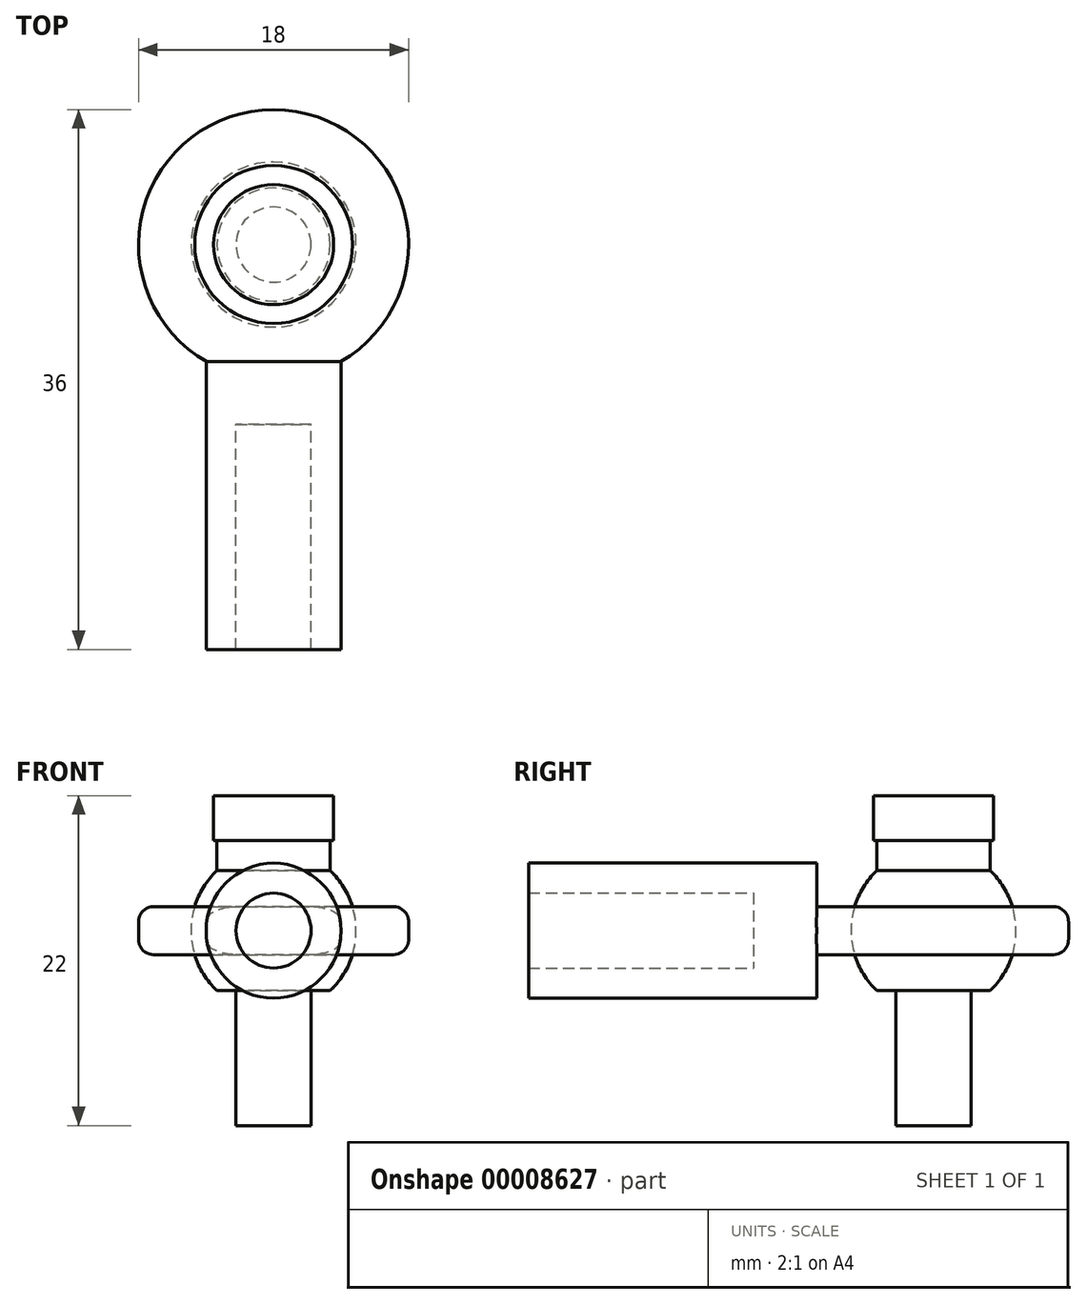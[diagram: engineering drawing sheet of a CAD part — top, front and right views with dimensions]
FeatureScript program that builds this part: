
annotation { "Feature Type Name" : "Feature", "Feature Type Description" : "" }
export const myFeature = defineFeature(function(context is Context, id is Id, definition is map)
    precondition{}
    {
        {
            var Q0;
            Q0=qCreatedBy(makeId("Right.planeOp"),FACE);
            var sketch = newSketch(context, id + "F0", { "sketchPlane" : qUnion([Q0])});
            skCircle(sketch, "E0", {"center": v(0, 0) * mm, "radius": 5.5 * mm});
            skLineSegment(sketch, "E1", {"start": v(-2.5, 4.9) * mm, "end": v(-2.5, -4.9) * mm});
            skLineSegment(sketch, "E2.MirrorCS", {"start": v(2.5, 4.9) * mm, "end": v(2.5, -4.9) * mm});
            skLineSegment(sketch, "E3", {"start": v(-2.5, 4) * mm, "end": v(-3.77, 4) * mm});
            skLineSegment(sketch, "E4.MirrorCS", {"start": v(-2.5, -4) * mm, "end": v(-3.77, -4) * mm});
            skLineSegment(sketch, "E5.MirrorCS", {"start": v(2.5, 4) * mm, "end": v(3.77, 4) * mm});
            skLineSegment(sketch, "E6.MirrorCS", {"start": v(2.5, -4) * mm, "end": v(3.77, -4) * mm});
            skLineSegment(sketch, "E7", {"start": v(0, 14.77) * mm, "end": v(0, -12.33) * mm, "construction": true});
            skLineSegment(sketch, "E8", {"start": v(-15.77, 0) * mm, "end": v(22.06, 0) * mm, "construction": true});
            skLineSegment(sketch, "E9", {"start": v(-9, 0) * mm, "end": v(-9, 1.6) * mm});
            skLineSegment(sketch, "E10", {"start": v(-9, 1.6) * mm, "end": v(-5.26, 1.6) * mm});
            skLineSegment(sketch, "E11.MirrorCS", {"start": v(-9, 0) * mm, "end": v(-9, -1.6) * mm});
            skLineSegment(sketch, "E12.MirrorCS", {"start": v(-9, -1.6) * mm, "end": v(-5.26, -1.6) * mm});
            skLineSegment(sketch, "E13.MirrorCS", {"start": v(9, 1.6) * mm, "end": v(5.26, 1.6) * mm});
            skLineSegment(sketch, "E14.MirrorCS", {"start": v(9, 0) * mm, "end": v(9, 1.6) * mm});
            skLineSegment(sketch, "E15.MirrorCS", {"start": v(9, 0) * mm, "end": v(9, -1.6) * mm});
            skLineSegment(sketch, "E16.MirrorCS", {"start": v(9, -1.6) * mm, "end": v(5.26, -1.6) * mm});
            skSolve(sketch);
        }
        {
            var Q0;
            {var subQ1=sQuery(id+"F0.wireOp",EDGE,"E3");Q0=makeQuery(id+"F0.imprint","IMPRINT",FACE,{"disambiguationData":[TD([[makeQuery(id+"F0.imprint","IMPRINT",EDGE,{"derivedFrom":subQ1}),1.0]])]});}
            var Q1;
            Q1=sQuery(id+"F0.wireOp",EDGE,"E7");
            revolve(context, id + "F1", {"entities" : qUnion([Q0]), "axis" : qUnion([Q1]), "revolveType" : RevolveType.FULL});
        }
        {
            var Q0;
            Q0=makeQuery(id+"F0.imprint","IMPRINT",FACE,{"disambiguationData":[TD([[makeQuery(id+"F0.imprint","IMPRINT",EDGE,{"derivedFrom":sQuery(id+"F0.wireOp",EDGE,"E9")}),-1.0]])]});
            var Q1;
            Q1=sQuery(id+"F0.wireOp",EDGE,"E7");
            revolve(context, id + "F2", {"entities" : qUnion([Q0]), "axis" : qUnion([Q1]), "revolveType" : RevolveType.FULL});
        }
        {
            var Q0;
            Q0=qCreatedBy(makeId("Top.planeOp"),FACE);
            var sketch = newSketch(context, id + "F3", { "sketchPlane" : qUnion([Q0])});
            skLineSegment(sketch, "E17", {"start": v(0, 0) * mm, "end": v(0, -27) * mm, "construction": true});
            skLineSegment(sketch, "E18", {"start": v(0, -27) * mm, "end": v(-4.5, -27) * mm});
            skLineSegment(sketch, "E19.MirrorCS", {"start": v(0, -27) * mm, "end": v(4.5, -27) * mm});
            skLineSegment(sketch, "E20", {"start": v(-2.5, -27) * mm, "end": v(-2.5, -12) * mm});
            skLineSegment(sketch, "E21", {"start": v(-2.5, -12) * mm, "end": v(0, -12) * mm});
            skLineSegment(sketch, "E22.MirrorCS", {"start": v(2.5, -12) * mm, "end": v(0, -12) * mm});
            skLineSegment(sketch, "E23.MirrorCS", {"start": v(2.5, -27) * mm, "end": v(2.5, -12) * mm});
            skCircle(sketch, "E24.0.0", {"center": v(0, 0) * mm, "radius": 9 * mm});
            skLineSegment(sketch, "E25", {"start": v(4.5, -27) * mm, "end": v(4.5, -7.8) * mm});
            skLineSegment(sketch, "E26", {"start": v(4.5, -7.8) * mm, "end": v(0, -7.8) * mm});
            skLineSegment(sketch, "E27.MirrorCS", {"start": v(-4.5, -7.8) * mm, "end": v(0, -7.8) * mm});
            skLineSegment(sketch, "E28.MirrorCS", {"start": v(-4.5, -27) * mm, "end": v(-4.5, -7.8) * mm});
            skLineSegment(sketch, "E29", {"start": v(0, -7.8) * mm, "end": v(0, -12) * mm});
            skSolve(sketch);
        }
        {
            var Q0;
            {var subQ3=sQuery(id+"F3.wireOp",EDGE,"E27.MirrorCS");Q0=makeQuery(id+"F3.imprint","IMPRINT",FACE,{"disambiguationData":[TD([[makeQuery(id+"F3.imprint","IMPRINT",EDGE,{"derivedFrom":subQ3}),-1.0]])]});}
            var Q1;
            {var subQ5=sQuery(id+"F3.wireOp",EDGE,"E20");Q1=makeQuery(id+"F3.imprint","IMPRINT",FACE,{"disambiguationData":[TD([[makeQuery(id+"F3.imprint","IMPRINT",EDGE,{"derivedFrom":subQ5}),1.0]])]});}
            var Q2;
            Q2=sQuery(id+"F3.wireOp",EDGE,"E17");
            revolve(context, id + "F4", {"operationType" : NewBodyOperationType.ADD, "entities" : qUnion([Q0, Q1]), "axis" : qUnion([Q2]), "revolveType" : RevolveType.FULL});
        }
        {
            var Q0;
            Q0=makeQuery(id+"F2.opRevolve","SWEPT_EDGE",EDGE,{"disambiguationData":[OSD([sQuery(id+"F0.wireOp",EDGE,"E9"),sQuery(id+"F0.wireOp",EDGE,"E10")])]});
            var Q1;
            Q1=makeQuery(id+"F2.opRevolve","SWEPT_EDGE",EDGE,{"disambiguationData":[OSD([sQuery(id+"F0.wireOp",EDGE,"E11.MirrorCS"),sQuery(id+"F0.wireOp",EDGE,"E12.MirrorCS")])]});
            fillet(context, id + "F5", {"entities" : qUnion([Q0, Q1]), "radius" : 1 * mm, "tangentPropagation" : true, "allowEdgeOverflow" : false});
        }
        {
            var Q0;
            Q0=makeQuery(id+"F1.opRevolve","SWEPT_FACE",FACE,{"disambiguationData":[OSD([sQuery(id+"F0.wireOp",EDGE,"E3")])]});
            extrude(context, id + "F6", {"entities" : qUnion([Q0]), "depth" : 2 * mm});
        }
        {
            var Q0;
            Q0=makeQuery(id+"F6.opExtrude","CAP_FACE",FACE,{"disambiguationData":[OSD([sQuery(id+"F0.wireOp",EDGE,"E3")])],"isStart":false});
            var sketch = newSketch(context, id + "F7", { "sketchPlane" : qUnion([Q0])});
            skCircle(sketch, "E30", {"center": v(0, 0) * mm, "radius": 2.5 * mm});
            skCircle(sketch, "E31", {"center": v(0, 0) * mm, "radius": 4 * mm});
            skSolve(sketch);
        }
        {
            var Q0;
            Q0=makeQuery(id+"F7.imprint","IMPRINT",FACE,{"disambiguationData":[TD([[makeQuery(id+"F7.imprint","IMPRINT",EDGE,{"derivedFrom":sQuery(id+"F7.wireOp",EDGE,"E31")}),1.0]])]});
            var Q1;
            Q1=makeQuery(id+"F7.imprint","IMPRINT",FACE,{"disambiguationData":[TD([[makeQuery(id+"F7.imprint","IMPRINT",EDGE,{"derivedFrom":sQuery(id+"F7.wireOp",EDGE,"E30")}),1.0]])]});
            var Q2;
            Q2=makeQuery(id+"F7.imprint","IMPRINT",FACE,{"disambiguationData":[TD([[makeQuery(id+"F7.imprint","IMPRINT",EDGE,{"derivedFrom":sQuery(id+"F7.wireOp",EDGE,"E30")}),-1.0]])]});
            extrude(context, id + "F8", {"entities" : qUnion([Q0, Q1, Q2]), "depth" : 3 * mm});
        }
        {
            var Q0;
            Q0=makeQuery(id+"F7.imprint","IMPRINT",FACE,{"disambiguationData":[TD([[makeQuery(id+"F7.imprint","IMPRINT",EDGE,{"derivedFrom":sQuery(id+"F7.wireOp",EDGE,"E30")}),1.0]])]});
            extrude(context, id + "F9", {"entities" : qUnion([Q0]), "operationType" : NewBodyOperationType.ADD, "oppositeDirection" : true, "depth" : 19 * mm});
        }
    });
